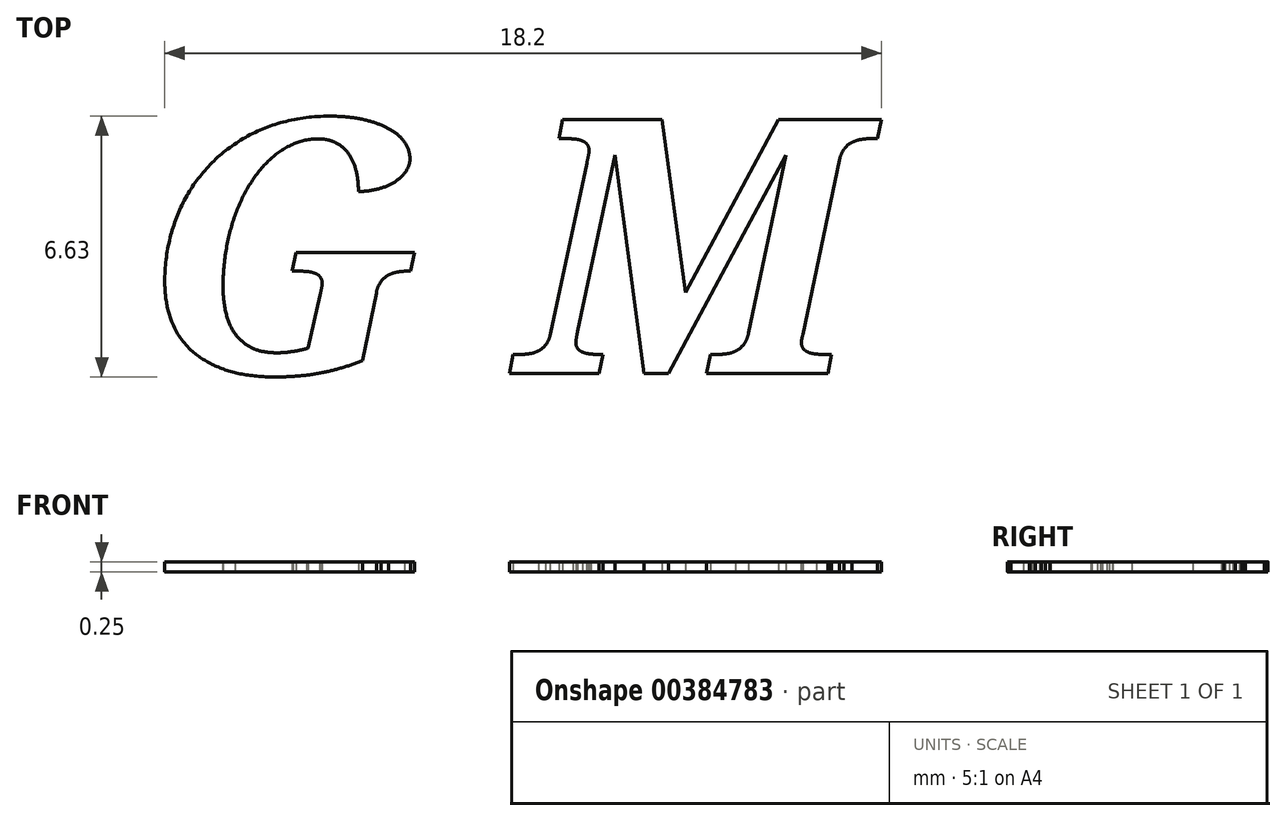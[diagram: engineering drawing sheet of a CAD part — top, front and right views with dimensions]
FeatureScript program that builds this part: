
annotation { "Feature Type Name" : "Feature", "Feature Type Description" : "" }
export const myFeature = defineFeature(function(context is Context, id is Id, definition is map)
    precondition{}
    {
        {
            var Q0;
            Q0=qCreatedBy(makeId("Top.planeOp"),FACE);
            var sketch = newSketch(context, id + "F0", { "sketchPlane" : qUnion([Q0])});
            skText(sketch, "E0", { "text": "G M", "fontName": "NotoSerif-BoldItalic.ttf"});
            const initialGuessF0  = {"E0": [-0.04798, 0.03637, 1, 0, 0.0065]};
            skSetInitialGuess(sketch, initialGuessF0);
            skSolve(sketch);
        }
        {
            var Q0;
            Q0 = qSketchRegion(id + "F0", true);
            extrude(context, id + "F1", {"entities" : qUnion([Q0]), "depth" : 0.25 * mm});
        }
    });
